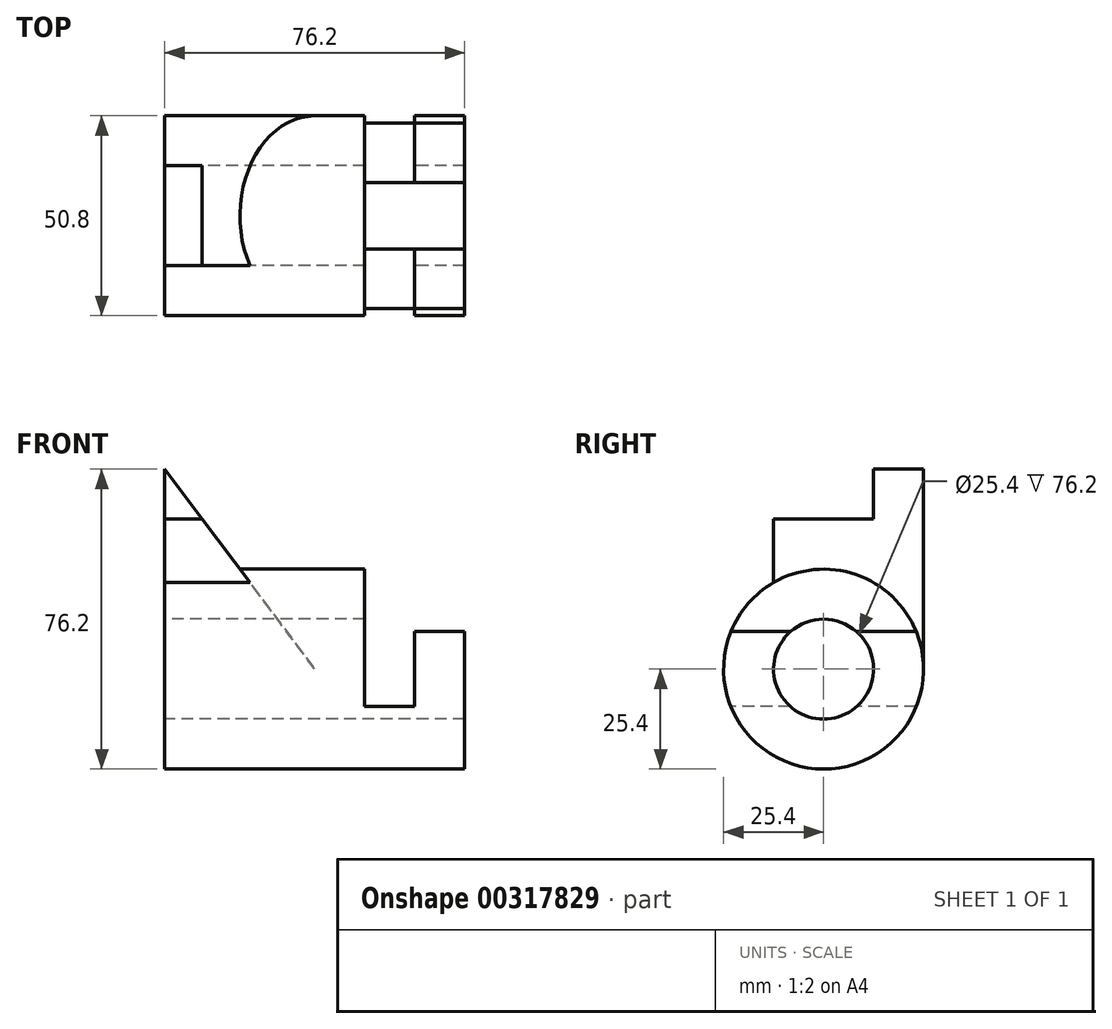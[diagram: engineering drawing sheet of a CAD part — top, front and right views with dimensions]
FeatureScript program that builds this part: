
annotation { "Feature Type Name" : "Feature", "Feature Type Description" : "" }
export const myFeature = defineFeature(function(context is Context, id is Id, definition is map)
    precondition{}
    {
        {
            var Q0;
            Q0=qCreatedBy(makeId("Right.planeOp"),FACE);
            var sketch = newSketch(context, id + "F0", { "sketchPlane" : qUnion([Q0])});
            skCircle(sketch, "E0", {"center": v(0, 0) * mm, "radius": 25.4 * mm});
            skCircle(sketch, "E1", {"center": v(0, 0) * mm, "radius": 12.7 * mm});
            skSolve(sketch);
        }
        {
            var Q0;
            Q0 = qSketchRegion(id + "F0", true);
            extrude(context, id + "F1", {"entities" : qUnion([Q0]), "depth" : 76.2 * mm});
        }
        {
            var Q0;
            Q0=makeQuery(id+"F1.opExtrude","CAP_FACE",FACE,{"disambiguationData":[OSD([sQuery(id+"F0.wireOp",EDGE,"E0"),sQuery(id+"F0.wireOp",EDGE,"E1")])],"isStart":false});
            var sketch = newSketch(context, id + "F2", { "sketchPlane" : qUnion([Q0])});
            skLineSegment(sketch, "E2", {"start": v(-8.4, 9.53) * mm, "end": v(-23.55, 9.53) * mm});
            skLineSegment(sketch, "E3", {"start": v(8.4, 9.53) * mm, "end": v(23.55, 9.53) * mm});
            skArc(sketch, "E4", {"start": v(23.55, 9.53) * mm, "mid": v(0, 25.4) * mm, "end": v(-23.55, 9.52) * mm});
            skArc(sketch, "E5", {"start": v(8.4, 9.53) * mm, "mid": v(0, 12.7) * mm, "end": v(-8.4, 9.53) * mm});
            skLineSegment(sketch, "E6", {"start": v(0, 31.15) * mm, "end": v(0, -34.56) * mm, "construction": true});
            skPoint(sketch, "E6.startSnap0", {"position": v(0, 25.4) * mm});
            skPoint(sketch, "E6.endSnap0", {"position": v(0, 25.4) * mm});
            skSolve(sketch);
        }
        {
            var Q0;
            Q0=makeQuery(id+"F2.imprint","IMPRINT",FACE,{"disambiguationData":[TD([[makeQuery(id+"F2.imprint","IMPRINT",EDGE,{"derivedFrom":sQuery(id+"F2.wireOp",EDGE,"E2")}),-1.0]])]});
            extrude(context, id + "F3", {"entities" : qUnion([Q0]), "operationType" : NewBodyOperationType.REMOVE, "oppositeDirection" : true, "depth" : 25.4 * mm});
        }
        {
            var Q0;
            Q0=qCreatedBy(makeId("Front.planeOp"),FACE);
            var sketch = newSketch(context, id + "F4", { "sketchPlane" : qUnion([Q0])});
            skLineSegment(sketch, "E7", {"start": v(63.5, 9.53) * mm, "end": v(63.5, -9.53) * mm});
            skLineSegment(sketch, "E8", {"start": v(63.5, -9.53) * mm, "end": v(50.8, -9.53) * mm});
            skLineSegment(sketch, "E9", {"start": v(50.8, -9.53) * mm, "end": v(50.8, 9.53) * mm});
            skLineSegment(sketch, "E10", {"start": v(50.8, 9.53) * mm, "end": v(63.5, 9.53) * mm});
            skLineSegment(sketch, "E11", {"start": v(0, 25.4) * mm, "end": v(79.33, 25.4) * mm, "construction": true});
            skSolve(sketch);
        }
        {
            var Q0;
            Q0 = qSketchRegion(id + "F4", true);
            extrude(context, id + "F5", {"entities" : qUnion([Q0]), "operationType" : NewBodyOperationType.REMOVE, "endBound" : BoundingType.THROUGH_ALL, "oppositeDirection" : true, "depth" : 25.4 * mm, "hasSecondDirection" : true, "secondDirectionBound" : SecondDirectionBoundingType.THROUGH_ALL, "secondDirectionOppositeDirection" : false, "secondDirectionDepth" : 25.4 * mm});
        }
        {
            var Q0;
            Q0=qCreatedBy(makeId("Front.planeOp"),FACE);
            var sketch = newSketch(context, id + "F6", { "sketchPlane" : qUnion([Q0])});
            skLineSegment(sketch, "E12", {"start": v(0, 0) * mm, "end": v(0, 50.8) * mm});
            skLineSegment(sketch, "E13", {"start": v(0, 0) * mm, "end": v(38.1, 0) * mm});
            skLineSegment(sketch, "E14", {"start": v(0, 50.8) * mm, "end": v(38.1, 0) * mm});
            skSolve(sketch);
        }
        {
            var Q0;
            Q0 = qSketchRegion(id + "F6", true);
            extrude(context, id + "F7", {"entities" : qUnion([Q0]), "operationType" : NewBodyOperationType.ADD, "endBound" : BoundingType.SYMMETRIC, "depth" : 50.8 * mm});
        }
        {
            var Q0;
            Q0=makeQuery(id+"F7.boolean.opBoolean","MERGE",FACE,{"derivedFrom":[makeQuery(id+"F1.opExtrude","CAP_FACE",FACE,{"disambiguationData":[OSD([sQuery(id+"F0.wireOp",EDGE,"E0"),sQuery(id+"F0.wireOp",EDGE,"E1")])],"isStart":true}),makeQuery(id+"F7.opExtrude","SWEPT_FACE",FACE,{"disambiguationData":[OSD([sQuery(id+"F6.wireOp",EDGE,"E12")])]})]});
            var sketch = newSketch(context, id + "F8", { "sketchPlane" : qUnion([Q0])});
            skCircle(sketch, "E15", {"center": v(0, 0) * mm, "radius": 12.7 * mm});
            skSolve(sketch);
        }
        {
            var Q0;
            Q0=makeQuery(id+"F8.imprint","IMPRINT",FACE,{"disambiguationData":[TD([[makeQuery(id+"F8.imprint","IMPRINT",EDGE,{"disambiguationData":[OD(0.0)],"derivedFrom":sQuery(id+"F8.wireOp",EDGE,"E15")}),1.0]])]});
            extrude(context, id + "F9", {"entities" : qUnion([Q0]), "operationType" : NewBodyOperationType.REMOVE, "endBound" : BoundingType.THROUGH_ALL, "oppositeDirection" : true, "depth" : 25.4 * mm});
        }
        {
            var Q0;
            Q0=makeQuery(id+"F7.opExtrude","CAP_FACE",FACE,{"disambiguationData":[OSD([sQuery(id+"F6.wireOp",EDGE,"E12"),sQuery(id+"F6.wireOp",EDGE,"E13"),sQuery(id+"F6.wireOp",EDGE,"E14")])],"isStart":false});
            var sketch = newSketch(context, id + "F10", { "sketchPlane" : qUnion([Q0])});
            skLineSegment(sketch, "E16", {"start": v(0, 50.8) * mm, "end": v(0, 38.1) * mm});
            skLineSegment(sketch, "E17", {"start": v(0, 38.1) * mm, "end": v(9.53, 38.1) * mm});
            skLineSegment(sketch, "E18", {"start": v(0, 50.8) * mm, "end": v(9.53, 38.1) * mm});
            skSolve(sketch);
        }
        {
            var Q0;
            Q0=makeQuery(id+"F10.imprint","IMPRINT",FACE,{"disambiguationData":[TD([[makeQuery(id+"F10.imprint","IMPRINT",EDGE,{"derivedFrom":sQuery(id+"F10.wireOp",EDGE,"E16")}),-1.0]])]});
            extrude(context, id + "F11", {"entities" : qUnion([Q0]), "operationType" : NewBodyOperationType.REMOVE, "oppositeDirection" : true, "depth" : 38.1 * mm});
        }
        {
            var Q0;
            Q0=makeQuery(id+"F7.boolean.opBoolean","MERGE",FACE,{"derivedFrom":[makeQuery(id+"F1.opExtrude","CAP_FACE",FACE,{"disambiguationData":[OSD([sQuery(id+"F0.wireOp",EDGE,"E0"),sQuery(id+"F0.wireOp",EDGE,"E1")])],"isStart":true}),makeQuery(id+"F7.opExtrude","SWEPT_FACE",FACE,{"disambiguationData":[OSD([sQuery(id+"F6.wireOp",EDGE,"E12")])]})]});
            var sketch = newSketch(context, id + "F12", { "sketchPlane" : qUnion([Q0])});
            skCircle(sketch, "E19", {"center": v(0, 0) * mm, "radius": 25.4 * mm});
            skLineSegment(sketch, "E20", {"start": v(25.4, 0) * mm, "end": v(25.4, 38.1) * mm});
            skLineSegment(sketch, "E21", {"start": v(25.4, 38.1) * mm, "end": v(12.7, 38.1) * mm});
            skLineSegment(sketch, "E22", {"start": v(12.7, 38.1) * mm, "end": v(12.7, 22) * mm});
            skSolve(sketch);
        }
        {
            var Q0;
            {var subQ0=sQuery(id+"F12.wireOp",EDGE,"E20");Q0=makeQuery(id+"F12.imprint","IMPRINT",FACE,{"disambiguationData":[TD([[makeQuery(id+"F12.imprint","IMPRINT",EDGE,{"derivedFrom":subQ0}),1.0]])]});}
            extrude(context, id + "F13", {"entities" : qUnion([Q0]), "operationType" : NewBodyOperationType.REMOVE, "endBound" : BoundingType.THROUGH_ALL, "oppositeDirection" : true, "depth" : 25.4 * mm});
        }
    });
